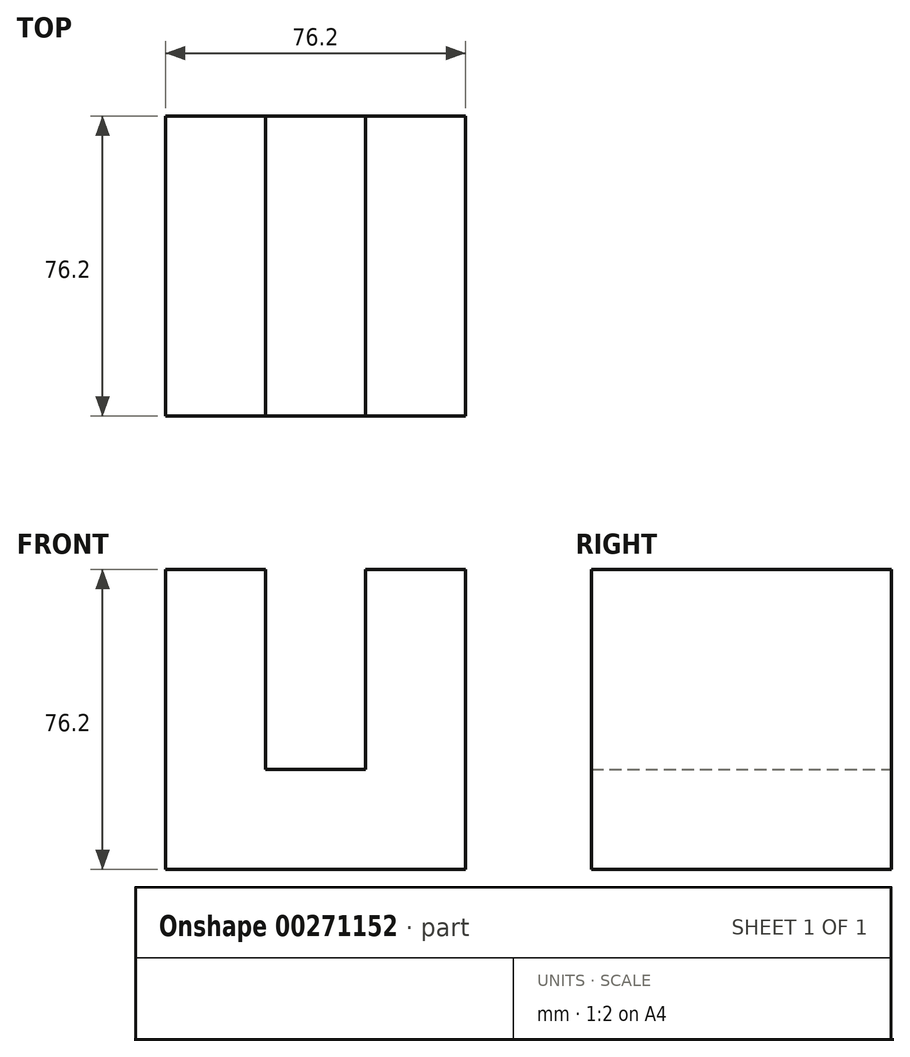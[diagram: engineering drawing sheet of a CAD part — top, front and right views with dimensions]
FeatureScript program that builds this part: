
annotation { "Feature Type Name" : "Feature", "Feature Type Description" : "" }
export const myFeature = defineFeature(function(context is Context, id is Id, definition is map)
    precondition{}
    {
        {
            var Q0;
            Q0=qCreatedBy(makeId("Front.planeOp"),FACE);
            var sketch = newSketch(context, id + "F0", { "sketchPlane" : qUnion([Q0])});
            skLineSegment(sketch, "E0", {"start": v(0, 0) * mm, "end": v(0, 76.2) * mm});
            skLineSegment(sketch, "E1", {"start": v(0, 76.2) * mm, "end": v(-25.4, 76.2) * mm});
            skLineSegment(sketch, "E2", {"start": v(-25.4, 76.2) * mm, "end": v(-25.4, 25.4) * mm});
            skLineSegment(sketch, "E3", {"start": v(-25.4, 25.4) * mm, "end": v(-50.8, 25.4) * mm});
            skLineSegment(sketch, "E4", {"start": v(-50.8, 25.4) * mm, "end": v(-50.8, 76.2) * mm});
            skLineSegment(sketch, "E5", {"start": v(-50.8, 76.2) * mm, "end": v(-76.2, 76.2) * mm});
            skLineSegment(sketch, "E6", {"start": v(-76.2, 76.2) * mm, "end": v(-76.2, 0) * mm});
            skLineSegment(sketch, "E7", {"start": v(-76.2, 0) * mm, "end": v(0, 0) * mm});
            skSolve(sketch);
        }
        {
            var Q0;
            Q0 = qSketchRegion(id + "F0", true);
            extrude(context, id + "F1", {"entities" : qUnion([Q0]), "depth" : 76.2 * mm});
        }
    });
